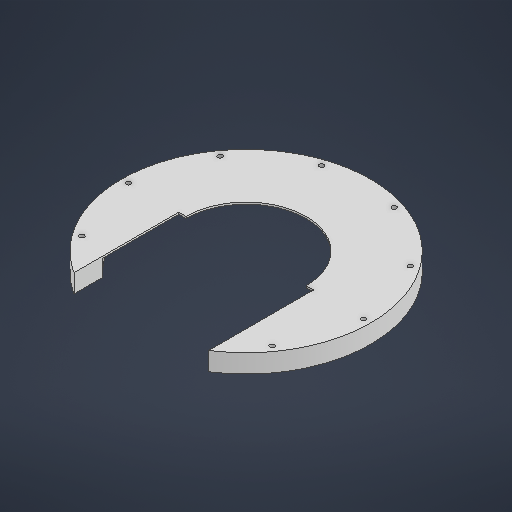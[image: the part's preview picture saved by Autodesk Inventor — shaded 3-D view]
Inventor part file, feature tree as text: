
AUTODESK INVENTOR PART (.ipt)
format: ipt  version: 2025 (Build 290162000, 162)  size: 235,008 bytes
history: native  units: in
note: dims shown in document units (in); Inventor stores cm internally (conversion verified against a paired STEP export)
features: sketch x5, extrude x3, hole x1
ambient origin geometry x8: Origin, YZ Plane, XZ Plane, XY Plane, X Axis, Y Axis, Z Axis, Center Point
bodies: Solid1 (feature_tree)
feature tree (9):
  extrude  "Extrusion1"  Depth=8.6614in
  hole  "Hole1"  [1 undecoded]
  extrude  "Extrusion3"  Depth=3.937in TaperAngle=360.0deg
  extrude  "Extrusion4"  Depth=0.315in
  sketch  "Sketch1"  dims[d0=10.6299in d1=8.6614in]
  sketch  "Sketch3"  dims[d8=0.1969in d9=3.937in d11=360.0deg]
  sketch  "Sketch Circular Pattern1"  dims[d2=0.7874in d3=0.0in d7=10.0394in]
  sketch  "Sketch4"  dims[d13=0.1969in d14=0.2362in d15=0.1575in d16=0.0787in d17=90.0deg d18=0.315in d19=0.8108in d21=5.1181in]
  sketch  "Sketch5"  dims[d22=0.0787in d23=0.0in d24=5.753in d25=13.7795in d26=0.0in d27=0.0in d28=0.0197in d29=0.0344in]
note: 1 required parameter value undecoded (feature->parameter linkage not recoverable at this tier; creation-order binding heuristic only, values carry confidence <= 0.55)
